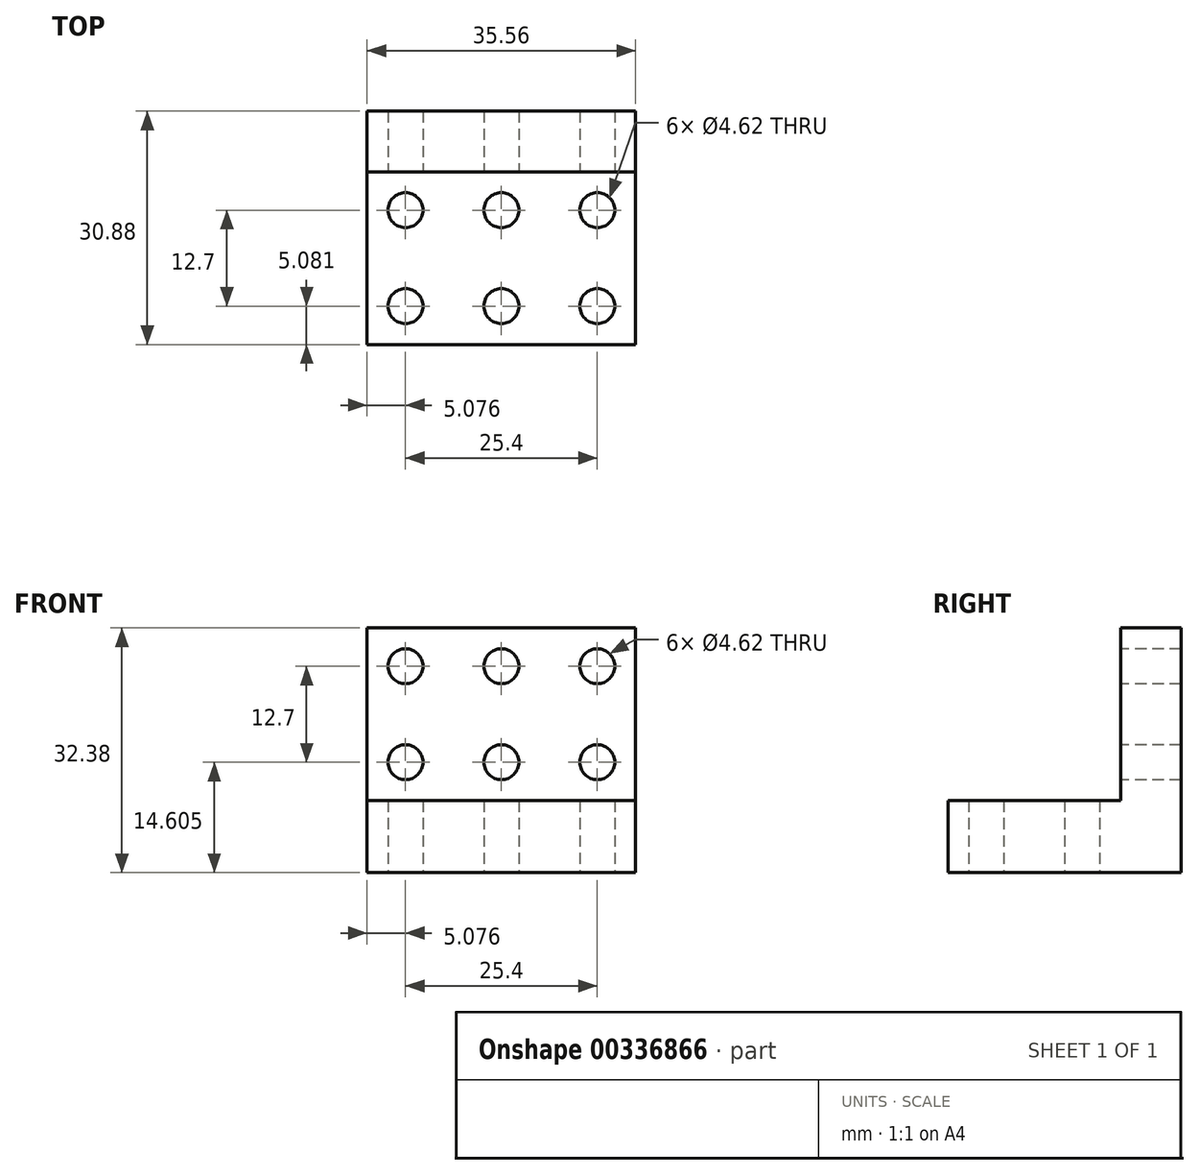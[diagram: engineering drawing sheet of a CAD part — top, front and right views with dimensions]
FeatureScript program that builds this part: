
annotation { "Feature Type Name" : "Feature", "Feature Type Description" : "" }
export const myFeature = defineFeature(function(context is Context, id is Id, definition is map)
    precondition{}
    {
        {
            var Q0;
            Q0=qCreatedBy(makeId("Top.planeOp"),FACE);
            var sketch = newSketch(context, id + "F0", { "sketchPlane" : qUnion([Q0])});
            skLineSegment(sketch, "E0.bottom", {"start": v(-45.83, 15.63) * mm, "end": v(-10.27, 15.63) * mm});
            skLineSegment(sketch, "E0.top", {"start": v(-45.83, -7.23) * mm, "end": v(-10.27, -7.23) * mm});
            skLineSegment(sketch, "E0.left", {"start": v(-45.83, 15.63) * mm, "end": v(-45.83, -7.23) * mm});
            skLineSegment(sketch, "E0.right", {"start": v(-10.27, 15.63) * mm, "end": v(-10.27, -7.23) * mm});
            skCircle(sketch, "E1", {"center": v(-40.75, 10.55) * mm, "radius": 2.31 * mm});
            skCircle(sketch, "E2.0.1.0", {"center": v(-40.75, -2.15) * mm, "radius": 2.31 * mm});
            skCircle(sketch, "E2.1.0.0", {"center": v(-28.05, 10.55) * mm, "radius": 2.31 * mm});
            skCircle(sketch, "E2.1.1.0", {"center": v(-28.05, -2.15) * mm, "radius": 2.31 * mm});
            skCircle(sketch, "E2.2.0.0", {"center": v(-15.35, 10.55) * mm, "radius": 2.31 * mm});
            skCircle(sketch, "E2.2.1.0", {"center": v(-15.35, -2.15) * mm, "radius": 2.31 * mm});
            skLineSegment(sketch, "E2.direction1", {"start": v(-40.75, 10.55) * mm, "end": v(-28.05, 10.55) * mm, "construction": true});
            skLineSegment(sketch, "E2.direction2", {"start": v(-40.75, 10.55) * mm, "end": v(-40.75, -2.15) * mm, "construction": true});
            skLineSegment(sketch, "E3", {"start": v(-45.83, 13.5) * mm, "end": v(-45.83, 23.65) * mm});
            skLineSegment(sketch, "E4", {"start": v(-45.83, 23.65) * mm, "end": v(-10.27, 23.65) * mm});
            skLineSegment(sketch, "E5", {"start": v(-10.27, 15.63) * mm, "end": v(-10.27, 23.65) * mm});
            skPoint(sketch, "E6.orphan", {"position": v(-9.54, 23.65) * mm});
            skSolve(sketch);
        }
        {
            var Q0;
            Q0=makeQuery(id+"F0.imprint","IMPRINT",FACE,{"disambiguationData":[TD([[makeQuery(id+"F0.imprint","IMPRINT",EDGE,{"derivedFrom":sQuery(id+"F0.wireOp",EDGE,"E0.bottom")}),-1.0]])]});
            extrude(context, id + "F1", {"entities" : qUnion([Q0]), "depth" : 9.52 * mm});
        }
        {
            var Q0;
            {var subQ0=sQuery(id+"F0.wireOp",EDGE,"E0.bottom");Q0=makeQuery(id+"F0.imprint","IMPRINT",FACE,{"disambiguationData":[TD([[makeQuery(id+"F0.imprint","IMPRINT",EDGE,{"derivedFrom":subQ0}),1.0]])]});}
            extrude(context, id + "F2", {"entities" : qUnion([Q0]), "operationType" : NewBodyOperationType.ADD, "depth" : 32.38 * mm});
        }
        {
            var Q0;
            Q0=makeQuery(id+"F2.opExtrude","SWEPT_FACE",FACE,{"disambiguationData":[OSD([sQuery(id+"F0.wireOp",EDGE,"E0.bottom")])]});
            var sketch = newSketch(context, id + "F3", { "sketchPlane" : qUnion([Q0])});
            skLineSegment(sketch, "E7.bottom", {"start": v(-45.83, 32.39) * mm, "end": v(-10.27, 32.39) * mm});
            skLineSegment(sketch, "E7.top", {"start": v(-45.83, 9.52) * mm, "end": v(-10.27, 9.52) * mm});
            skLineSegment(sketch, "E7.left", {"start": v(-45.83, 32.39) * mm, "end": v(-45.83, 9.52) * mm});
            skLineSegment(sketch, "E7.right", {"start": v(-10.27, 32.39) * mm, "end": v(-10.27, 9.52) * mm});
            skCircle(sketch, "E8", {"center": v(-40.75, 27.3) * mm, "radius": 2.31 * mm});
            skCircle(sketch, "E9.0.1.0", {"center": v(-40.75, 14.6) * mm, "radius": 2.31 * mm});
            skCircle(sketch, "E9.1.0.0", {"center": v(-28.05, 27.3) * mm, "radius": 2.31 * mm});
            skCircle(sketch, "E9.1.1.0", {"center": v(-28.05, 14.6) * mm, "radius": 2.31 * mm});
            skCircle(sketch, "E9.2.0.0", {"center": v(-15.35, 27.3) * mm, "radius": 2.31 * mm});
            skCircle(sketch, "E9.2.1.0", {"center": v(-15.35, 14.6) * mm, "radius": 2.31 * mm});
            skLineSegment(sketch, "E9.direction1", {"start": v(-40.75, 27.3) * mm, "end": v(-28.05, 27.3) * mm, "construction": true});
            skLineSegment(sketch, "E9.direction2", {"start": v(-40.75, 27.3) * mm, "end": v(-40.75, 14.6) * mm, "construction": true});
            skSolve(sketch);
        }
        {
            var Q0;
            Q0=makeQuery(id+"F3.imprint","IMPRINT",FACE,{"disambiguationData":[TD([[makeQuery(id+"F3.imprint","IMPRINT",EDGE,{"derivedFrom":sQuery(id+"F3.wireOp",EDGE,"E8")}),1.0]])]});
            var Q1;
            Q1=makeQuery(id+"F3.imprint","IMPRINT",FACE,{"disambiguationData":[TD([[makeQuery(id+"F3.imprint","IMPRINT",EDGE,{"derivedFrom":sQuery(id+"F3.wireOp",EDGE,"E9.1.0.0")}),1.0]])]});
            var Q2;
            Q2=makeQuery(id+"F3.imprint","IMPRINT",FACE,{"disambiguationData":[TD([[makeQuery(id+"F3.imprint","IMPRINT",EDGE,{"derivedFrom":sQuery(id+"F3.wireOp",EDGE,"E9.2.0.0")}),1.0]])]});
            var Q3;
            Q3=makeQuery(id+"F3.imprint","IMPRINT",FACE,{"disambiguationData":[TD([[makeQuery(id+"F3.imprint","IMPRINT",EDGE,{"derivedFrom":sQuery(id+"F3.wireOp",EDGE,"E9.2.1.0")}),1.0]])]});
            var Q4;
            Q4=makeQuery(id+"F3.imprint","IMPRINT",FACE,{"disambiguationData":[TD([[makeQuery(id+"F3.imprint","IMPRINT",EDGE,{"derivedFrom":sQuery(id+"F3.wireOp",EDGE,"E9.1.1.0")}),1.0]])]});
            var Q5;
            Q5=makeQuery(id+"F3.imprint","IMPRINT",FACE,{"disambiguationData":[TD([[makeQuery(id+"F3.imprint","IMPRINT",EDGE,{"derivedFrom":sQuery(id+"F3.wireOp",EDGE,"E9.0.1.0")}),1.0]])]});
            extrude(context, id + "F4", {"entities" : qUnion([Q0, Q1, Q2, Q3, Q4, Q5]), "operationType" : NewBodyOperationType.REMOVE, "oppositeDirection" : true, "depth" : 25.4 * mm});
        }
    });
